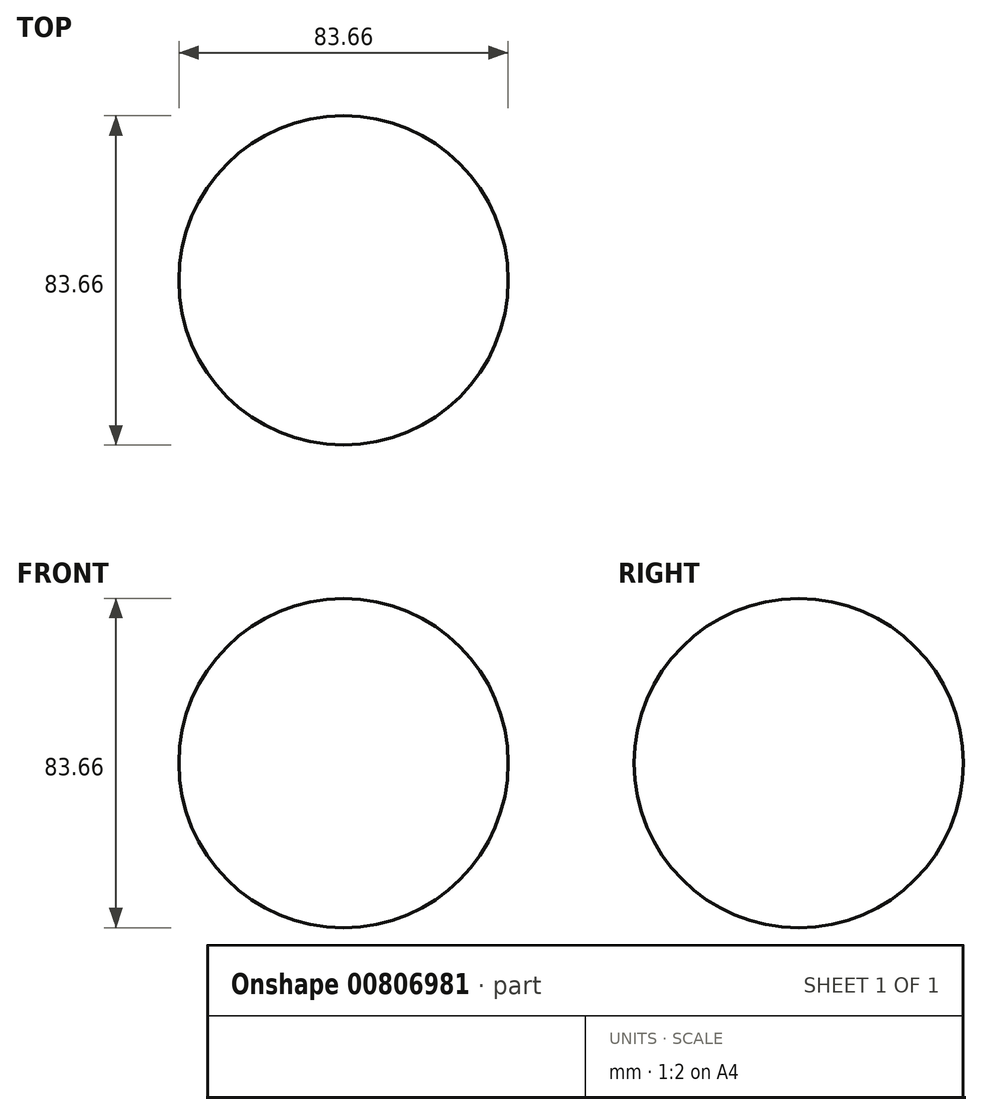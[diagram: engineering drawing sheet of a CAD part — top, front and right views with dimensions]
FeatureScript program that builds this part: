
annotation { "Feature Type Name" : "Feature", "Feature Type Description" : "" }
export const myFeature = defineFeature(function(context is Context, id is Id, definition is map)
    precondition{}
    {
        {
            var Q0;
            Q0=qCreatedBy(makeId("Front.planeOp"),FACE);
            var sketch = newSketch(context, id + "F0", { "sketchPlane" : qUnion([Q0])});
            skCircle(sketch, "E0", {"center": v(0, 0) * mm, "radius": 41.83 * mm});
            skLineSegment(sketch, "E1", {"start": v(0, 65.27) * mm, "end": v(0, -72.73) * mm});
            skSolve(sketch);
        }
        {
            var Q0;
            {var subQ0=sQuery(id+"F0.wireOp",EDGE,"E1");var subQ1=sQuery(id+"F0.wireOp",EDGE,"E0");var subQ2=makeQuery(id+"F0.imprint","INTERSECT",VERTEX,{"disambiguationData":[OD(0.0)],"derivedFrom":[subQ1,subQ0]});Q0=makeQuery(id+"F0.imprint","IMPRINT",FACE,{"disambiguationData":[TD([[makeQuery(id+"F0.imprint","IMPRINT",EDGE,{"disambiguationData":[TD([[subQ2,1.0]])],"derivedFrom":subQ1}),1.0]])]});}
            var Q1;
            Q1=sQuery(id+"F0.wireOp",EDGE,"E1");
            revolve(context, id + "F1", {"surfaceOperationType" : NewSurfaceOperationType.NEW, "entities" : qUnion([Q0]), "axis" : qUnion([Q1]), "revolveType" : RevolveType.FULL});
        }
    });
